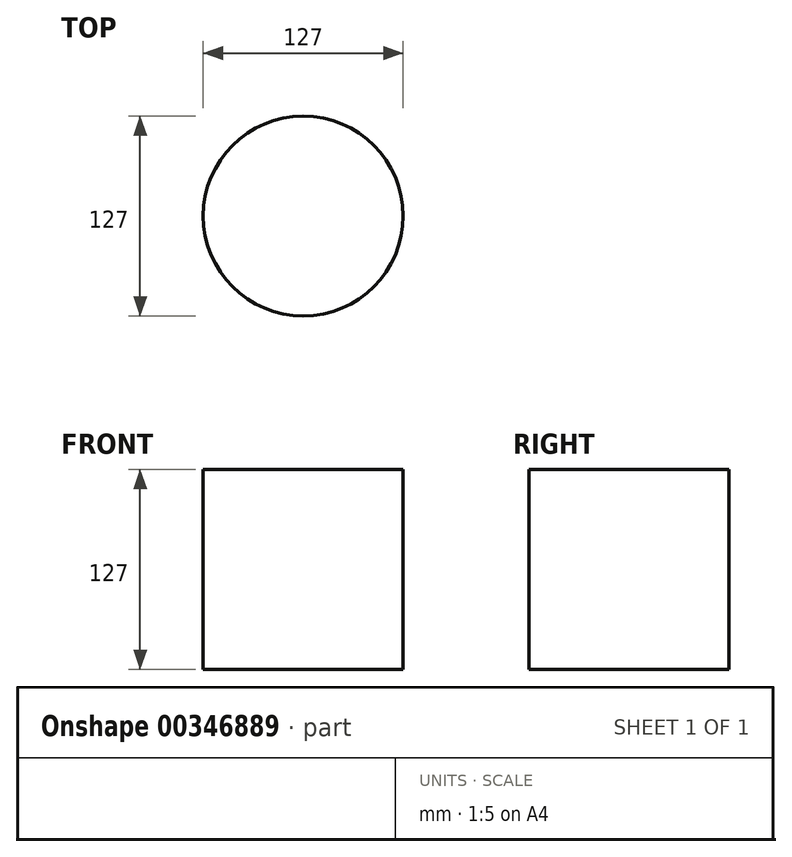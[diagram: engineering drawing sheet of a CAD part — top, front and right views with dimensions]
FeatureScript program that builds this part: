
annotation { "Feature Type Name" : "Feature", "Feature Type Description" : "" }
export const myFeature = defineFeature(function(context is Context, id is Id, definition is map)
    precondition{}
    {
        {
            var Q0;
            Q0=qCreatedBy(makeId("Top.planeOp"),FACE);
            var sketch = newSketch(context, id + "F0", { "sketchPlane" : qUnion([Q0])});
            skCircle(sketch, "E0", {"center": v(0, 0) * mm, "radius": 63.5 * mm});
            skSolve(sketch);
        }
        {
            var Q0;
            Q0=sQuery(id+"F0.wireOp",EDGE,"E0");
            extrude(context, id + "F1", {"bodyType" : ToolBodyType.SURFACE, "surfaceEntities" : qUnion([Q0]), "depth" : 127 * mm});
        }
    });
